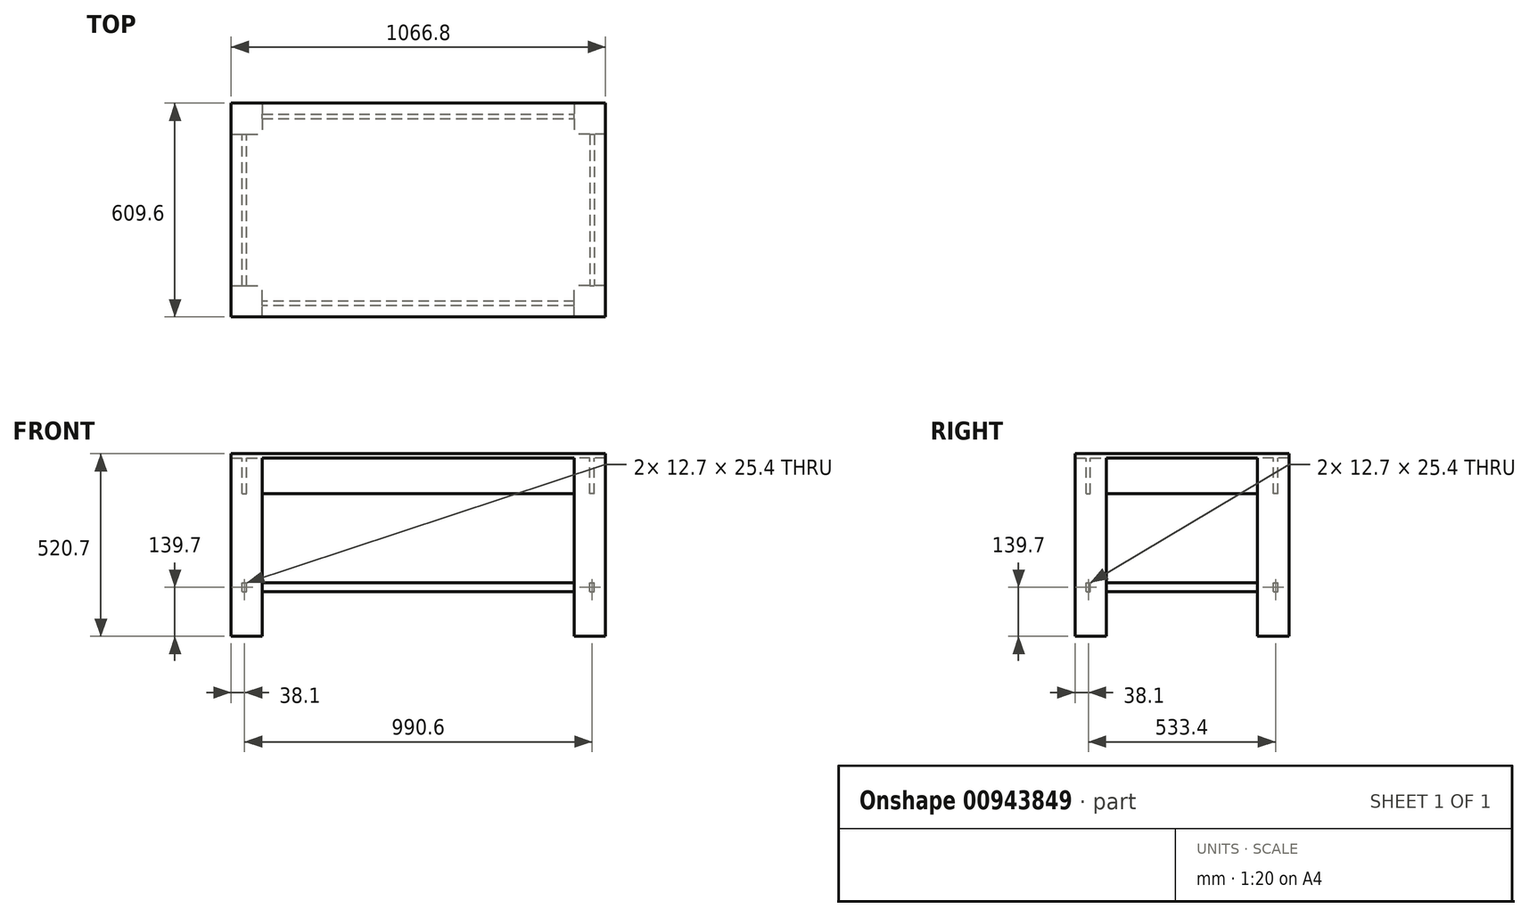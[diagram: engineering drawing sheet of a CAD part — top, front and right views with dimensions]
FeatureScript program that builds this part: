
annotation { "Feature Type Name" : "Feature", "Feature Type Description" : "" }
export const myFeature = defineFeature(function(context is Context, id is Id, definition is map)
    precondition{}
    {
        {
            var Q0;
            Q0=qCreatedBy(makeId("Top.planeOp"),FACE);
            var sketch = newSketch(context, id + "F0", { "sketchPlane" : qUnion([Q0])});
            skLineSegment(sketch, "E0.bottom", {"start": v(-533.4, 304.8) * mm, "end": v(533.4, 304.8) * mm});
            skLineSegment(sketch, "E0.top", {"start": v(-533.4, -304.8) * mm, "end": v(533.4, -304.8) * mm});
            skLineSegment(sketch, "E0.left", {"start": v(-533.4, 304.8) * mm, "end": v(-533.4, -304.8) * mm});
            skLineSegment(sketch, "E0.right", {"start": v(533.4, 304.8) * mm, "end": v(533.4, -304.8) * mm});
            skPoint(sketch, "E0.middle", {"position": v(0, 0) * mm});
            skLineSegment(sketch, "E1.bottom", {"start": v(-533.4, 304.8) * mm, "end": v(-444.5, 304.8) * mm});
            skLineSegment(sketch, "E1.top", {"start": v(-533.4, 215.9) * mm, "end": v(-444.5, 215.9) * mm});
            skLineSegment(sketch, "E1.left", {"start": v(-533.4, 304.8) * mm, "end": v(-533.4, 215.9) * mm});
            skLineSegment(sketch, "E1.right", {"start": v(-444.5, 304.8) * mm, "end": v(-444.5, 215.9) * mm});
            skLineSegment(sketch, "E2.bottom", {"start": v(533.4, 304.8) * mm, "end": v(444.5, 304.8) * mm});
            skLineSegment(sketch, "E2.top", {"start": v(533.4, 215.9) * mm, "end": v(444.5, 215.9) * mm});
            skLineSegment(sketch, "E2.left", {"start": v(533.4, 304.8) * mm, "end": v(533.4, 215.9) * mm});
            skLineSegment(sketch, "E2.right", {"start": v(444.5, 304.8) * mm, "end": v(444.5, 215.9) * mm});
            skLineSegment(sketch, "E3.bottom", {"start": v(533.4, -304.8) * mm, "end": v(444.5, -304.8) * mm});
            skLineSegment(sketch, "E3.top", {"start": v(533.4, -215.9) * mm, "end": v(444.5, -215.9) * mm});
            skLineSegment(sketch, "E3.left", {"start": v(533.4, -304.8) * mm, "end": v(533.4, -215.9) * mm});
            skLineSegment(sketch, "E3.right", {"start": v(444.5, -304.8) * mm, "end": v(444.5, -215.9) * mm});
            skLineSegment(sketch, "E4.bottom", {"start": v(-533.4, -304.8) * mm, "end": v(-444.5, -304.8) * mm});
            skLineSegment(sketch, "E4.top", {"start": v(-533.4, -215.9) * mm, "end": v(-444.5, -215.9) * mm});
            skLineSegment(sketch, "E4.left", {"start": v(-533.4, -304.8) * mm, "end": v(-533.4, -215.9) * mm});
            skLineSegment(sketch, "E4.right", {"start": v(-444.5, -304.8) * mm, "end": v(-444.5, -215.9) * mm});
            skSolve(sketch);
        }
        {
            var Q0;
            {var subQ3=sQuery(id+"F0.wireOp",EDGE,"E1.top");Q0=makeQuery(id+"F0.imprint","IMPRINT",FACE,{"disambiguationData":[TD([[makeQuery(id+"F0.imprint","IMPRINT",EDGE,{"derivedFrom":subQ3}),-1.0]])]});}
            extrude(context, id + "F1", {"entities" : qUnion([Q0]), "depth" : 12.7 * mm, "offsetDistance" : 25.4 * mm});
        }
        {
            var Q0;
            {var subQ4=sQuery(id+"F0.wireOp",EDGE,"E1.top");Q0=makeQuery(id+"F0.imprint","IMPRINT",FACE,{"disambiguationData":[TD([[makeQuery(id+"F0.imprint","IMPRINT",EDGE,{"derivedFrom":subQ4}),1.0]])]});}
            var Q1;
            {var subQ4=sQuery(id+"F0.wireOp",EDGE,"E4.top");Q1=makeQuery(id+"F0.imprint","IMPRINT",FACE,{"disambiguationData":[TD([[makeQuery(id+"F0.imprint","IMPRINT",EDGE,{"derivedFrom":subQ4}),-1.0]])]});}
            var Q2;
            {var subQ4=sQuery(id+"F0.wireOp",EDGE,"E2.top");Q2=makeQuery(id+"F0.imprint","IMPRINT",FACE,{"disambiguationData":[TD([[makeQuery(id+"F0.imprint","IMPRINT",EDGE,{"derivedFrom":subQ4}),-1.0]])]});}
            var Q3;
            {var subQ4=sQuery(id+"F0.wireOp",EDGE,"E3.top");Q3=makeQuery(id+"F0.imprint","IMPRINT",FACE,{"disambiguationData":[TD([[makeQuery(id+"F0.imprint","IMPRINT",EDGE,{"derivedFrom":subQ4}),1.0]])]});}
            extrude(context, id + "F2", {"entities" : qUnion([Q0, Q1, Q2, Q3]), "operationType" : NewBodyOperationType.ADD, "depth" : 12.7 * mm, "offsetDistance" : 25.4 * mm, "hasSecondDirection" : true, "secondDirectionOppositeDirection" : true, "secondDirectionDepth" : 508 * mm});
        }
        {
            var Q0;
            Q0=makeQuery(id+"F1.opExtrude","CAP_FACE",FACE,{"disambiguationData":[OSD([sQuery(id+"F0.wireOp",EDGE,"E0.bottom"),sQuery(id+"F0.wireOp",EDGE,"E0.top"),sQuery(id+"F0.wireOp",EDGE,"E0.left"),sQuery(id+"F0.wireOp",EDGE,"E0.right"),sQuery(id+"F0.wireOp",EDGE,"E1.top"),sQuery(id+"F0.wireOp",EDGE,"E1.right"),sQuery(id+"F0.wireOp",EDGE,"E2.top"),sQuery(id+"F0.wireOp",EDGE,"E2.right"),sQuery(id+"F0.wireOp",EDGE,"E3.top"),sQuery(id+"F0.wireOp",EDGE,"E3.right"),sQuery(id+"F0.wireOp",EDGE,"E4.top"),sQuery(id+"F0.wireOp",EDGE,"E4.right")])],"isStart":true});
            var sketch = newSketch(context, id + "F3", { "sketchPlane" : qUnion([Q0])});
            skLineSegment(sketch, "E5.0.0", {"start": v(444.5, -304.8) * mm, "end": v(444.5, -215.9) * mm});
            skLineSegment(sketch, "E5.0.1", {"start": v(444.5, -215.9) * mm, "end": v(533.4, -215.9) * mm});
            skLineSegment(sketch, "E5.0.2", {"start": v(533.4, -215.9) * mm, "end": v(533.4, 215.9) * mm});
            skLineSegment(sketch, "E5.0.3", {"start": v(533.4, 215.9) * mm, "end": v(444.5, 215.9) * mm});
            skLineSegment(sketch, "E5.0.4", {"start": v(444.5, 215.9) * mm, "end": v(444.5, 304.8) * mm});
            skLineSegment(sketch, "E5.0.5", {"start": v(444.5, 304.8) * mm, "end": v(-444.5, 304.8) * mm});
            skLineSegment(sketch, "E5.0.6", {"start": v(-444.5, 304.8) * mm, "end": v(-444.5, 215.9) * mm});
            skLineSegment(sketch, "E5.0.7", {"start": v(-444.5, 215.9) * mm, "end": v(-533.4, 215.9) * mm});
            skLineSegment(sketch, "E5.0.8", {"start": v(-533.4, 215.9) * mm, "end": v(-533.4, -215.9) * mm});
            skLineSegment(sketch, "E5.0.9", {"start": v(-533.4, -215.9) * mm, "end": v(-444.5, -215.9) * mm});
            skLineSegment(sketch, "E5.0.10", {"start": v(-444.5, -215.9) * mm, "end": v(-444.5, -304.8) * mm});
            skLineSegment(sketch, "E5.0.11", {"start": v(-444.5, -304.8) * mm, "end": v(444.5, -304.8) * mm});
            skLineSegment(sketch, "E6.bottom", {"start": v(444.5, 260.35) * mm, "end": v(-444.5, 260.35) * mm});
            skLineSegment(sketch, "E6.top", {"start": v(444.5, 273.05) * mm, "end": v(-444.5, 273.05) * mm});
            skLineSegment(sketch, "E6.left", {"start": v(444.5, 260.35) * mm, "end": v(444.5, 273.05) * mm});
            skLineSegment(sketch, "E6.right", {"start": v(-444.5, 260.35) * mm, "end": v(-444.5, 273.05) * mm});
            skLineSegment(sketch, "E7.bottom", {"start": v(-488.95, 215.9) * mm, "end": v(-501.65, 215.9) * mm});
            skLineSegment(sketch, "E7.top", {"start": v(-488.95, -215.9) * mm, "end": v(-501.65, -215.9) * mm});
            skLineSegment(sketch, "E7.left", {"start": v(-488.95, 215.9) * mm, "end": v(-488.95, -215.9) * mm});
            skLineSegment(sketch, "E7.right", {"start": v(-501.65, 215.9) * mm, "end": v(-501.65, -215.9) * mm});
            skLineSegment(sketch, "E8.bottom", {"start": v(-444.5, -260.35) * mm, "end": v(444.5, -260.35) * mm});
            skLineSegment(sketch, "E8.top", {"start": v(-444.5, -273.05) * mm, "end": v(444.5, -273.05) * mm});
            skLineSegment(sketch, "E8.left", {"start": v(-444.5, -260.35) * mm, "end": v(-444.5, -273.05) * mm});
            skLineSegment(sketch, "E8.right", {"start": v(444.5, -260.35) * mm, "end": v(444.5, -273.05) * mm});
            skLineSegment(sketch, "E9.bottom", {"start": v(488.95, -215.9) * mm, "end": v(501.65, -215.9) * mm});
            skLineSegment(sketch, "E9.top", {"start": v(488.95, 215.9) * mm, "end": v(501.65, 215.9) * mm});
            skLineSegment(sketch, "E9.left", {"start": v(488.95, -215.9) * mm, "end": v(488.95, 215.9) * mm});
            skLineSegment(sketch, "E9.right", {"start": v(501.65, -215.9) * mm, "end": v(501.65, 215.9) * mm});
            skSolve(sketch);
        }
        {
            var Q0;
            {var subQ0=sQuery(id+"F3.wireOp",EDGE,"E6.bottom");Q0=makeQuery(id+"F3.imprint","IMPRINT",FACE,{"disambiguationData":[TD([[makeQuery(id+"F3.imprint","IMPRINT",EDGE,{"derivedFrom":subQ0}),-1.0]])]});}
            var Q1;
            {var subQ0=sQuery(id+"F3.wireOp",EDGE,"E7.left");Q1=makeQuery(id+"F3.imprint","IMPRINT",FACE,{"disambiguationData":[TD([[makeQuery(id+"F3.imprint","IMPRINT",EDGE,{"derivedFrom":subQ0}),-1.0]])]});}
            var Q2;
            {var subQ0=sQuery(id+"F3.wireOp",EDGE,"E8.bottom");Q2=makeQuery(id+"F3.imprint","IMPRINT",FACE,{"disambiguationData":[TD([[makeQuery(id+"F3.imprint","IMPRINT",EDGE,{"derivedFrom":subQ0}),-1.0]])]});}
            var Q3;
            {var subQ0=sQuery(id+"F3.wireOp",EDGE,"E9.left");Q3=makeQuery(id+"F3.imprint","IMPRINT",FACE,{"disambiguationData":[TD([[makeQuery(id+"F3.imprint","IMPRINT",EDGE,{"derivedFrom":subQ0}),-1.0]])]});}
            extrude(context, id + "F4", {"entities" : qUnion([Q0, Q1, Q2, Q3]), "operationType" : NewBodyOperationType.ADD, "depth" : 101.6 * mm, "offsetDistance" : 25.4 * mm});
        }
        {
            var Q0;
            Q0=makeQuery(id+"F2.opExtrude","CAP_FACE",FACE,{"disambiguationData":[OSD([sQuery(id+"F0.wireOp",EDGE,"E0.top"),sQuery(id+"F0.wireOp",EDGE,"E0.left"),sQuery(id+"F0.wireOp",EDGE,"E4.top"),sQuery(id+"F0.wireOp",EDGE,"E4.right")])],"isStart":true});
            cPlane(context, id + "F5", {"entities" : qUnion([Q0]), "cplaneType" : CPlaneType.OFFSET, "offset" : 152.4 * mm, "oppositeDirection" : true, "width" : 152.4 * mm, "height" : 152.4 * mm});
        }
        {
            var Q0;
            Q0=qCreatedBy(id+"F5.planeOp",FACE);
            var sketch = newSketch(context, id + "F6", { "sketchPlane" : qUnion([Q0])});
            skLineSegment(sketch, "E10.0", {"start": v(-444.5, 304.8) * mm, "end": v(-444.5, 215.9) * mm});
            skLineSegment(sketch, "E10.1", {"start": v(444.5, 304.8) * mm, "end": v(444.5, 215.9) * mm});
            skLineSegment(sketch, "E11.bottom", {"start": v(-444.5, 260.35) * mm, "end": v(444.5, 260.35) * mm});
            skLineSegment(sketch, "E11.top", {"start": v(-444.5, 273.05) * mm, "end": v(444.5, 273.05) * mm});
            skLineSegment(sketch, "E11.left", {"start": v(-444.5, 260.35) * mm, "end": v(-444.5, 273.05) * mm});
            skLineSegment(sketch, "E11.right", {"start": v(444.5, 260.35) * mm, "end": v(444.5, 273.05) * mm});
            skLineSegment(sketch, "E12.MirrorCS", {"start": v(-444.5, -260.35) * mm, "end": v(444.5, -260.35) * mm});
            skLineSegment(sketch, "E13.MirrorCS", {"start": v(-444.5, -273.05) * mm, "end": v(444.5, -273.05) * mm});
            skLineSegment(sketch, "E14.0", {"start": v(-533.4, 215.9) * mm, "end": v(-444.5, 215.9) * mm});
            skLineSegment(sketch, "E14.1", {"start": v(-533.4, -215.9) * mm, "end": v(-444.5, -215.9) * mm});
            skLineSegment(sketch, "E15.bottom", {"start": v(-488.95, 215.9) * mm, "end": v(-501.65, 215.9) * mm});
            skLineSegment(sketch, "E15.top", {"start": v(-488.95, -215.9) * mm, "end": v(-501.65, -215.9) * mm});
            skLineSegment(sketch, "E15.left", {"start": v(-488.95, 215.9) * mm, "end": v(-488.95, -215.9) * mm});
            skLineSegment(sketch, "E15.right", {"start": v(-501.65, 215.9) * mm, "end": v(-501.65, -215.9) * mm});
            skLineSegment(sketch, "E16.MirrorCS", {"start": v(488.95, -215.9) * mm, "end": v(501.65, -215.9) * mm});
            skLineSegment(sketch, "E17.MirrorCS", {"start": v(488.95, 215.9) * mm, "end": v(501.65, 215.9) * mm});
            skLineSegment(sketch, "E18.MirrorCS", {"start": v(501.65, 215.9) * mm, "end": v(501.65, -215.9) * mm});
            skLineSegment(sketch, "E19.MirrorCS", {"start": v(488.95, 215.9) * mm, "end": v(488.95, -215.9) * mm});
            skLineSegment(sketch, "E20.MirrorCS", {"start": v(444.5, -260.35) * mm, "end": v(444.5, -273.05) * mm});
            skLineSegment(sketch, "E21.MirrorCS", {"start": v(-444.5, -260.35) * mm, "end": v(-444.5, -273.05) * mm});
            skSolve(sketch);
        }
        {
            var Q0;
            {var subQ0=sQuery(id+"F6.wireOp",EDGE,"E15.left");var subQ4=sQuery(id+"F6.wireOp",EDGE,"E11.bottom");Q0=qUnion([makeQuery(id+"F6.imprint","IMPRINT",FACE,{"disambiguationData":[TD([[makeQuery(id+"F6.imprint","IMPRINT",EDGE,{"derivedFrom":subQ4}),1.0]])]}),makeQuery(id+"F6.imprint","IMPRINT",FACE,{"disambiguationData":[TD([[makeQuery(id+"F6.imprint","IMPRINT",EDGE,{"derivedFrom":sQuery(id+"F6.wireOp",EDGE,"E12.MirrorCS")}),-1.0]])]}),makeQuery(id+"F6.imprint","IMPRINT",FACE,{"disambiguationData":[TD([[makeQuery(id+"F6.imprint","IMPRINT",EDGE,{"derivedFrom":subQ0}),-1.0]])]}),makeQuery(id+"F6.imprint","IMPRINT",FACE,{"disambiguationData":[TD([[makeQuery(id+"F6.imprint","IMPRINT",EDGE,{"derivedFrom":sQuery(id+"F6.wireOp",EDGE,"E16.MirrorCS")}),1.0]])]})]);}
            extrude(context, id + "F7", {"entities" : qUnion([Q0]), "operationType" : NewBodyOperationType.ADD, "depth" : 25.4 * mm, "offsetDistance" : 25.4 * mm});
        }
    });
